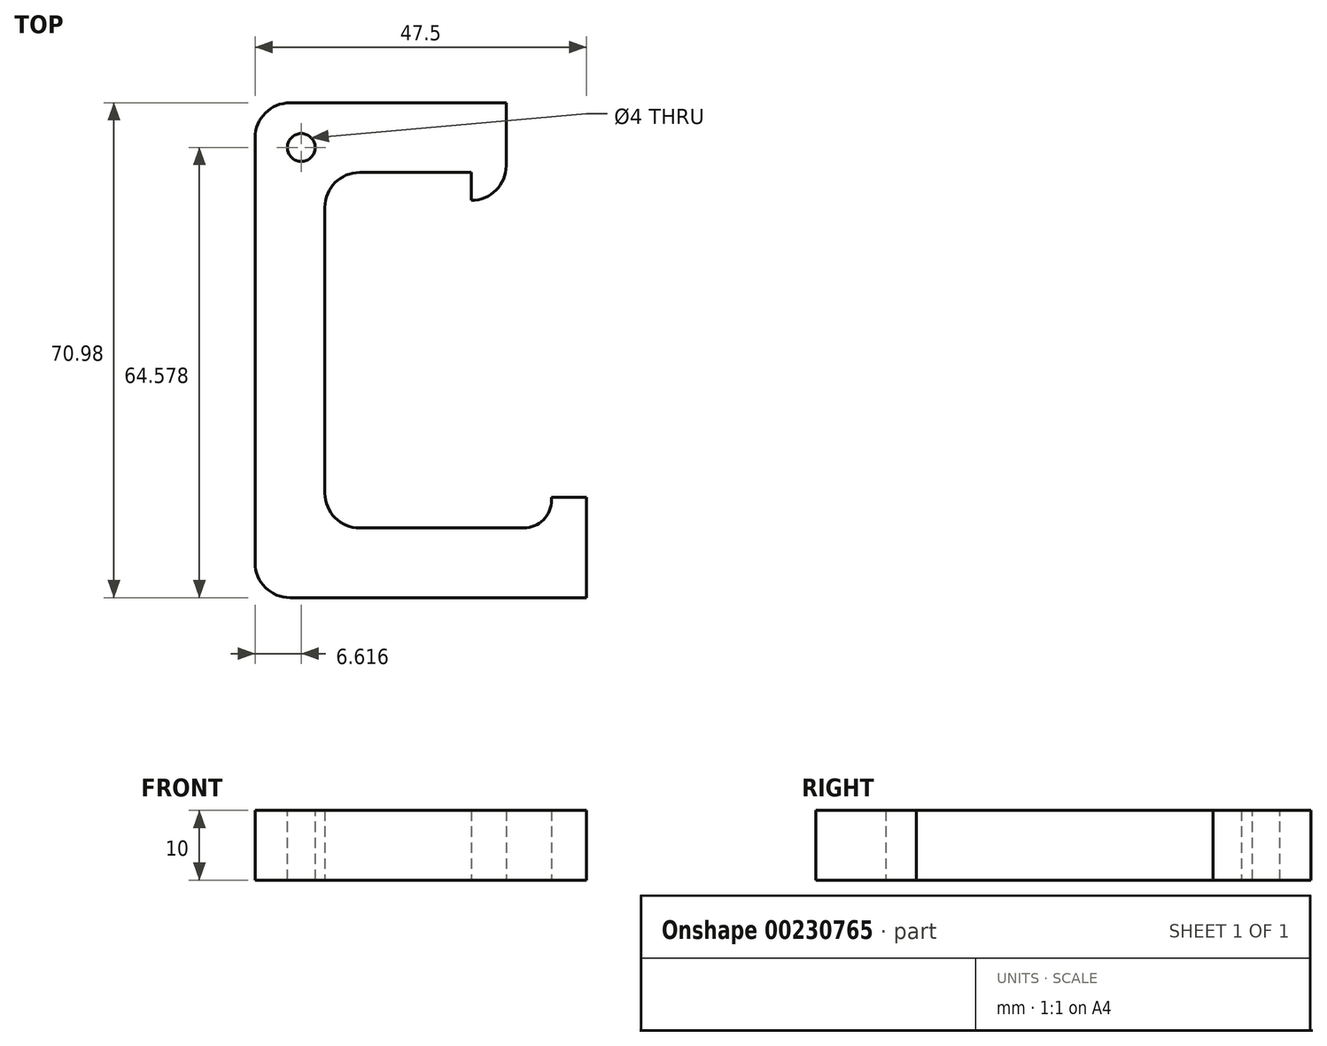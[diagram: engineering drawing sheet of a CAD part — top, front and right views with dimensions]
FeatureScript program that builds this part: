
annotation { "Feature Type Name" : "Feature", "Feature Type Description" : "" }
export const myFeature = defineFeature(function(context is Context, id is Id, definition is map)
    precondition{}
    {
        {
            var Q0;
            Q0=qCreatedBy(makeId("Top.planeOp"),FACE);
            var sketch = newSketch(context, id + "F0", { "sketchPlane" : qUnion([Q0])});
            skLineSegment(sketch, "E0", {"start": v(0, 0) * mm, "end": v(0, 70.98) * mm});
            skLineSegment(sketch, "E1", {"start": v(0, 70.98) * mm, "end": v(36, 70.98) * mm});
            skLineSegment(sketch, "E2", {"start": v(36, 70.98) * mm, "end": v(36, 56.98) * mm});
            skLineSegment(sketch, "E3", {"start": v(10, 61) * mm, "end": v(10, 10) * mm});
            skLineSegment(sketch, "E4", {"start": v(10, 10) * mm, "end": v(36, 10) * mm});
            skLineSegment(sketch, "E5", {"start": v(36, 0) * mm, "end": v(0, 0) * mm});
            skLineSegment(sketch, "E6", {"start": v(26.88, 61) * mm, "end": v(10, 61) * mm});
            skLineSegment(sketch, "E7", {"start": v(36, 56.98) * mm, "end": v(31, 56.98) * mm});
            skLineSegment(sketch, "E8", {"start": v(26.88, 61) * mm, "end": v(31, 61) * mm});
            skLineSegment(sketch, "E9", {"start": v(31, 61) * mm, "end": v(31, 56.98) * mm});
            skLineSegment(sketch, "E10", {"start": v(36, 10) * mm, "end": v(42.5, 10) * mm});
            skLineSegment(sketch, "E11", {"start": v(42.5, 10) * mm, "end": v(42.5, 14.4) * mm});
            skLineSegment(sketch, "E12", {"start": v(42.5, 14.4) * mm, "end": v(47.5, 14.4) * mm});
            skLineSegment(sketch, "E13", {"start": v(47.5, 14.4) * mm, "end": v(47.5, 0) * mm});
            skLineSegment(sketch, "E14", {"start": v(47.5, 0) * mm, "end": v(36, 0) * mm});
            skSolve(sketch);
        }
        {
            var Q0;
            Q0=makeQuery(id+"F0.imprint","IMPRINT",FACE,{"disambiguationData":[TD([[makeQuery(id+"F0.imprint","IMPRINT",EDGE,{"derivedFrom":sQuery(id+"F0.wireOp",EDGE,"E0")}),-1.0]])]});
            extrude(context, id + "F1", {"entities" : qUnion([Q0]), "depth" : 10 * mm});
        }
        {
            var Q0;
            Q0=makeQuery(id+"F1.opExtrude","SWEPT_EDGE",EDGE,{"disambiguationData":[OSD([sQuery(id+"F0.wireOp",EDGE,"E0"),sQuery(id+"F0.wireOp",EDGE,"E5")])]});
            var Q1;
            Q1=makeQuery(id+"F1.opExtrude","SWEPT_EDGE",EDGE,{"disambiguationData":[OSD([sQuery(id+"F0.wireOp",EDGE,"E0"),sQuery(id+"F0.wireOp",EDGE,"E1")])]});
            fillet(context, id + "F2", {"entities" : qUnion([Q0, Q1]), "radius" : 5 * mm, "tangentPropagation" : true, "allowEdgeOverflow" : false});
        }
        {
            var Q0;
            Q0=makeQuery(id+"F1.opExtrude","SWEPT_EDGE",EDGE,{"disambiguationData":[OSD([sQuery(id+"F0.wireOp",EDGE,"E3"),sQuery(id+"F0.wireOp",EDGE,"E4")])]});
            var Q1;
            Q1=makeQuery(id+"F1.opExtrude","SWEPT_EDGE",EDGE,{"disambiguationData":[OSD([sQuery(id+"F0.wireOp",EDGE,"cyD3rfWM-QoYb-Qv6v-N9PO-cr1qxgxEyCI0"),sQuery(id+"F0.wireOp",EDGE,"E3")])]});
            fillet(context, id + "F3", {"entities" : qUnion([Q0, Q1]), "radius" : 5 * mm, "tangentPropagation" : true, "allowEdgeOverflow" : false});
        }
        {
            var Q0;
            Q0=makeQuery(id+"F1.opExtrude","SWEPT_EDGE",EDGE,{"disambiguationData":[OSD([sQuery(id+"F0.wireOp",EDGE,"E2"),sQuery(id+"F0.wireOp",EDGE,"E7")])]});
            fillet(context, id + "F4", {"entities" : qUnion([Q0]), "radius" : 5 * mm, "tangentPropagation" : true, "allowEdgeOverflow" : false});
        }
        {
            var Q0;
            Q0=makeQuery(id+"F1.opExtrude","SWEPT_EDGE",EDGE,{"disambiguationData":[OSD([sQuery(id+"F0.wireOp",EDGE,"E10"),sQuery(id+"F0.wireOp",EDGE,"E11")])]});
            fillet(context, id + "F5", {"entities" : qUnion([Q0]), "radius" : 4 * mm, "tangentPropagation" : true, "allowEdgeOverflow" : false});
        }
        {
            var Q0;
            Q0=makeQuery(id+"F1.opExtrude","CAP_FACE",FACE,{"disambiguationData":[OSD([sQuery(id+"F0.wireOp",EDGE,"E0"),sQuery(id+"F0.wireOp",EDGE,"E1"),sQuery(id+"F0.wireOp",EDGE,"E2"),sQuery(id+"F0.wireOp",EDGE,"E3"),sQuery(id+"F0.wireOp",EDGE,"E4"),sQuery(id+"F0.wireOp",EDGE,"E5"),sQuery(id+"F0.wireOp",EDGE,"E6"),sQuery(id+"F0.wireOp",EDGE,"E7"),sQuery(id+"F0.wireOp",EDGE,"E8"),sQuery(id+"F0.wireOp",EDGE,"E9"),sQuery(id+"F0.wireOp",EDGE,"E10"),sQuery(id+"F0.wireOp",EDGE,"E11"),sQuery(id+"F0.wireOp",EDGE,"E12"),sQuery(id+"F0.wireOp",EDGE,"E13"),sQuery(id+"F0.wireOp",EDGE,"E14")])],"isStart":false});
            var sketch = newSketch(context, id + "F6", { "sketchPlane" : qUnion([Q0])});
            skCircle(sketch, "E15", {"center": v(6.62, 64.58) * mm, "radius": 2 * mm});
            skSolve(sketch);
        }
        {
            var Q0;
            Q0 = qSketchRegion(id + "F6", true);
            extrude(context, id + "F7", {"entities" : qUnion([Q0]), "operationType" : NewBodyOperationType.REMOVE, "endBound" : BoundingType.UP_TO_NEXT, "oppositeDirection" : true, "depth" : 10 * mm});
        }
    });
